# Revit family: IMBER
name_source: partatom
category: Lighting Fixtures
revit_build: Autodesk Revit Architecture 2015 (Build: 20140322_1515(x64)
units: mm (PartAtom-declared; Revit-internal decimal feet)

## types (2) — shared parameters
Apparent Load = 1 VA
Color Filter = 16777215
Dimming Lamp Color Temperature Shift = <None>
Emit Shape Visible in Rendering = Yes
Emit from Circle Diameter = 21 mm
IP = IP65
Klasyfikacja obciążenia = Oświetlenie
Kąt rozsyłu = 105°
Lamp = LED
Manufacturer = KANLUX
Materiał klosz = KANLUX - klosz - tworzywo sztuczne
Materiał obudowa = KANLUX - obudowa - stop aluminium, srebrny
Moc oprawy = 1 W
Photometric Web File = IMBER LED NW.ies
Tilt Angle = 90.00°
URL = www.kanlux.pl
Wattage Comments = 1
Współczynnik mocy = 1
Wysokość = 16 mm
Średnica = 30 mm
Średnica otworu = 27 mm
zero-valued in all types: Default Elevation

## per-type parameters (varying)
| type | Kod | Model |
| KANLUX IMBER LED NW 23520 LED 4000K 105° 40lm srebrny | 23520 | IMBER LED NW |
| KANLUX IMBER LED CW 23521 LED 6500K 105° 40lm srebny | 23521 | IMBER LED CW |
